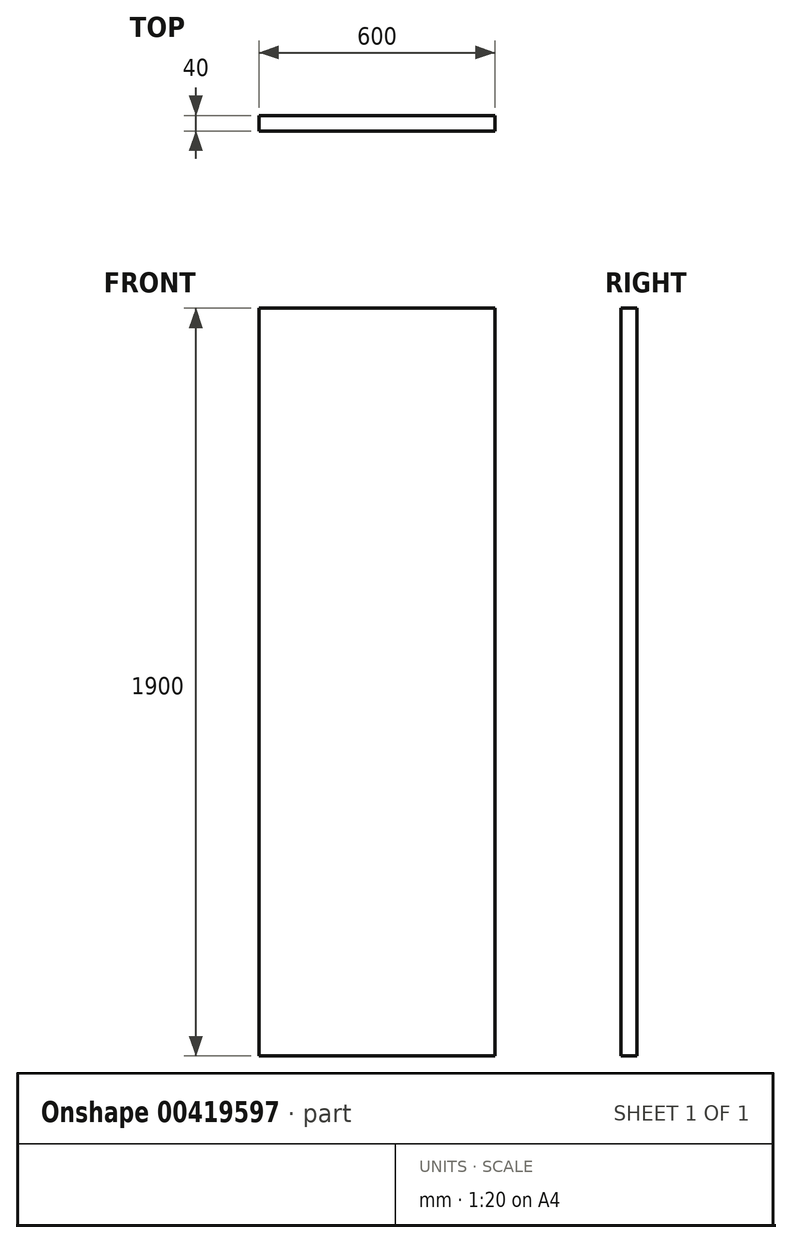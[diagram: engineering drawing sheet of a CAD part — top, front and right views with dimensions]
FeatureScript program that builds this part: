
annotation { "Feature Type Name" : "Feature", "Feature Type Description" : "" }
export const myFeature = defineFeature(function(context is Context, id is Id, definition is map)
    precondition{}
    {
        {
            var Q0;
            Q0=qCreatedBy(makeId("Top.planeOp"),FACE);
            var sketch = newSketch(context, id + "F0", { "sketchPlane" : qUnion([Q0])});
            skLineSegment(sketch, "E0.bottom", {"start": v(-545.74, 51.88) * mm, "end": v(54.26, 51.88) * mm});
            skLineSegment(sketch, "E0.top", {"start": v(-545.74, 11.88) * mm, "end": v(54.26, 11.88) * mm});
            skLineSegment(sketch, "E0.left", {"start": v(-545.74, 51.88) * mm, "end": v(-545.74, 11.88) * mm});
            skLineSegment(sketch, "E0.right", {"start": v(54.26, 51.88) * mm, "end": v(54.26, 11.88) * mm});
            skSolve(sketch);
        }
        {
            var Q0;
            Q0=makeQuery(id+"F0.imprint","IMPRINT",FACE,{"disambiguationData":[TD([[makeQuery(id+"F0.imprint","IMPRINT",EDGE,{"derivedFrom":sQuery(id+"F0.wireOp",EDGE,"E0.bottom")}),-1.0]])]});
            extrude(context, id + "F1", {"entities" : qUnion([Q0]), "depth" : 1900 * mm});
        }
    });
